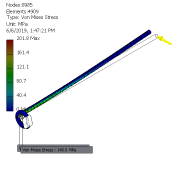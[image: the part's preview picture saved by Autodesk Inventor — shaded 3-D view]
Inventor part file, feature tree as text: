
AUTODESK INVENTOR PART (.ipt)
format: ipt  version: 2017 (Build 210142000, 142)  size: 120,320 bytes
history: native  units: mm
features: sketch x3, plane x1, extrude x1, sweep x1
ambient origin geometry x8: Origin, YZ Plane, XZ Plane, XY Plane, X Axis, Y Axis, Z Axis, Center Point
bodies: Body1 (feature_tree)
feature tree (6):
  plane  "Work Plane1"
  extrude  "Extrusion1"  Depth=8.0mm
  sweep  "Sweep2"
  sketch  "Sketch4"  dims[d4=30.0mm d8=8.0mm]
  sketch  "Sketch5"  dims[d9=365.0mm d10=0.0mm d11=30.0mm]
  sketch  "Sketch6"  dims[d12=0.0mm d13=0.0mm]
